# Revit family: Hitachi_RAC-E25_E35YHA_Outdoor_Unit_0718
name_source: partatom
category: Mechanical Equipment
revit_build: Autodesk Revit 2015 (Build: 20140223_1515(x64)
units: mm (PartAtom-declared; Revit-internal decimal feet)

## types (2) — shared parameters
Back Clearance = 50 mm  [stored 0.164042 ft]
Clearance = Default
Front Clearance = 300 mm
Height Refig Pipe (Top LIQUID) = 163 mm
Height Refrig Pipe (Bottom - GAS) = 91 mm  [stored 0.298556 ft]
Interconnecting Wires = 3 + E, 1.5 mm
Left Clearance = 100 mm  [stored 0.328084 ft]
Manufacturer = Temperzone / Hitachi
Material = Hitachi - Outdoor Unit
Outdoor Operating Temp. (cooling) C db = 46 to -10 C
Outdoor Operating Temp. (heating) C db = 21 to -15 C
Pipe Connection Size - Gas = 9.5 mm
Pipe Connection Size - Liquid = 6.35 mm
Pipe Height (max.) = 10m
Pipe Length (min./max.) = 3m to 20m
Power Suppy = 240 / 1
Radius Pipe Bottom GAS = 5 mm  [stored 0.0164042 ft]
Radius pipe Top LIQUID = 3 mm  [stored 0.00984252 ft]
Recommended External Protection = 15 A
Refrig Pipe Offset from Back = 202 mm  [stored 0.66273 ft]
Refrigerant Pipe Charge Length = 20m
Refrigerant Type = R32
Right Clearance = 200 mm  [stored 0.656168 ft]
Top Clearance = 200 mm  [stored 0.656168 ft]
URL = www.temperzone.biz
Unit Depth = 288 mm  [stored 0.944882 ft]
Unit Height = 548 mm  [stored 1.7979 ft]
Unit Width = 750 mm  [stored 2.46063 ft]
Weight (kg) = 34

## per-type parameters (varying)
| type | Airflow - Hi | COP Heating | Cooling Capacity | Cooling Range | Description | EER Cooling | Heating Capacity | Heating Range | Model - Indoor | Sound Pressure Level (dbA) - Cool / Heat |
| RAC-E25YHA | 158.0 L/s | 4.74 | 2500 W | 0.9 - 3.1 kW | Hitachi Outdoor Unit RAC-E25YHA | 4.51 | 3200 W | 0.9 - 4.4 kW | RAS-E25YHA | 46 / 47 |
| RAC-E35YHA | 217.0 L/s | 4.23 | 3500 W | 0.9 - 4.0 kW | Hitachi Outdoor Unit RAC-E35YHA | 3.75 | 4000 W | 0.9 - 5.0 kW | RAS-E35YHA | 47 / 48 |

note: column(s) folded — value = type name in every type: Model

note: [stored X ft] marks values corroborated as IEEE doubles in the binary element streams (Revit-internal decimal feet)

## geometry (parser evidence)
native form markers: Blend x4, Sweep x2
no freeform markers — native parametric forms only
